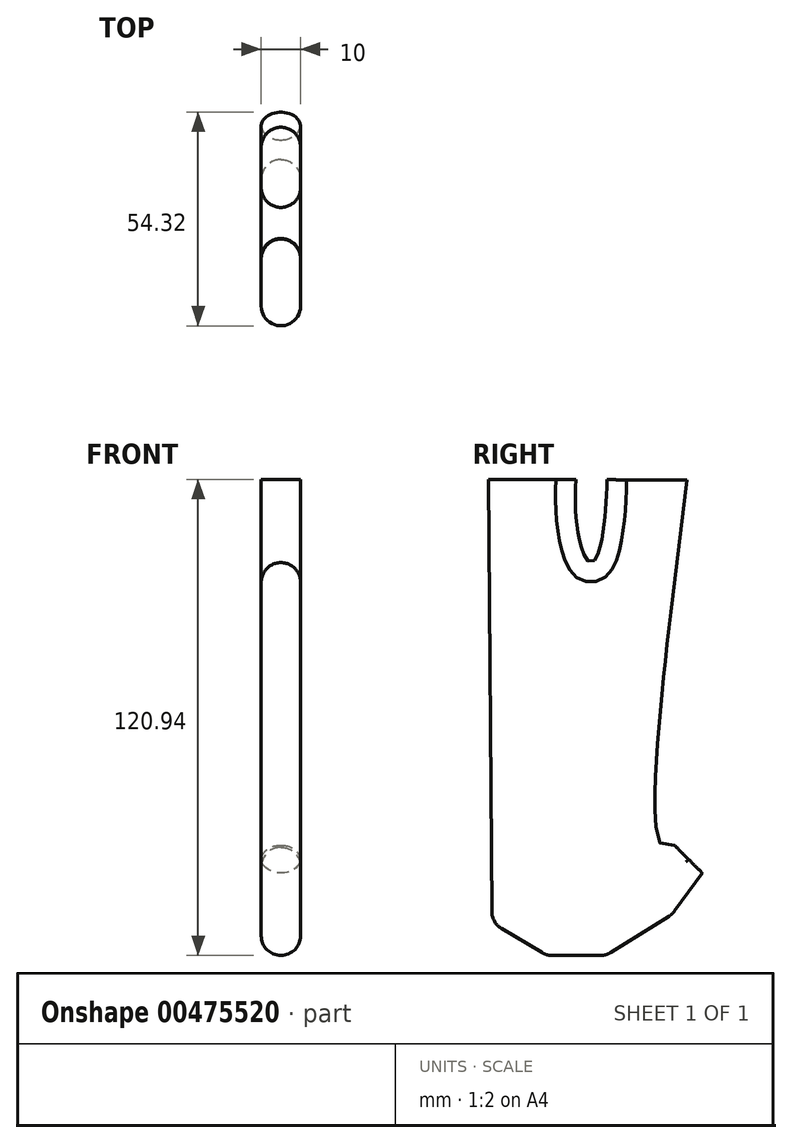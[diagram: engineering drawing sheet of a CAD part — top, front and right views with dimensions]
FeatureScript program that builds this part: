
annotation { "Feature Type Name" : "Feature", "Feature Type Description" : "" }
export const myFeature = defineFeature(function(context is Context, id is Id, definition is map)
    precondition{}
    {
        {
            var Q0;
            Q0=qCreatedBy(makeId("Top.planeOp"),FACE);
            var sketch = newSketch(context, id + "F0", { "sketchPlane" : qUnion([Q0])});
            skLineSegment(sketch, "E0.bottom", {"start": v(50, 50) * mm, "end": v(-50, 50) * mm});
            skLineSegment(sketch, "E0.top", {"start": v(50, -50) * mm, "end": v(-50, -50) * mm});
            skLineSegment(sketch, "E0.left", {"start": v(50, 50) * mm, "end": v(50, -50) * mm});
            skLineSegment(sketch, "E0.right", {"start": v(-50, 50) * mm, "end": v(-50, -50) * mm});
            skPoint(sketch, "E0.middle", {"position": v(0, 0) * mm});
            skSolve(sketch);
        }
        {
            var Q0;
            Q0=qCreatedBy(makeId("Right.planeOp"),FACE);
            var sketch = newSketch(context, id + "F1", { "sketchPlane" : qUnion([Q0])});
            skLineSegment(sketch, "E1", {"start": v(32.93, -92.93) * mm, "end": v(40, -100) * mm});
            skLineSegment(sketch, "E2", {"start": v(40, -100) * mm, "end": v(50, -100) * mm});
            skLineSegment(sketch, "E3", {"start": v(50, -100) * mm, "end": v(50, 0) * mm});
            skLineSegment(sketch, "E4", {"start": v(40, -100) * mm, "end": v(32.42, -110.44) * mm});
            skLineSegment(sketch, "E5", {"start": v(32.42, -110.44) * mm, "end": v(15.56, -120.94) * mm});
            skLineSegment(sketch, "E6", {"start": v(15.56, -120.94) * mm, "end": v(0.42, -120.94) * mm});
            skLineSegment(sketch, "E7", {"start": v(0.42, -120.94) * mm, "end": v(-13.45, -112.58) * mm});
            skLineSegment(sketch, "E8", {"start": v(-13.45, -112.58) * mm, "end": v(-14.32, 0) * mm});
            skLineSegment(sketch, "E9", {"start": v(7.9, -0.07) * mm, "end": v(-14.32, 0) * mm});
            skLineSegment(sketch, "E10", {"start": v(15.79, -0.07) * mm, "end": v(36.15, -0.14) * mm});
            skFitSpline(sketch, "E11", {"points": [v(32.93, -92.93) * mm, v(29.65, -92.93) * mm, v(36.15, -0.14) * mm], "startDerivative": vector(-23, -8.71) * mm, "endDerivative": vector(19.71, 156.62) * mm});
            skFitSpline(sketch, "E12", {"points": [v(15.79, -0.07) * mm, v(11.46, -21.08) * mm, v(7.9, -0.07) * mm], "startDerivative": vector(-1.65, -83.3) * mm, "endDerivative": vector(4.4, 67.18) * mm});
            skSolve(sketch);
        }
        {
            var Q0;
            Q0=makeQuery(id+"F1.imprint","IMPRINT",FACE,{"disambiguationData":[TD([[makeQuery(id+"F1.imprint","IMPRINT",EDGE,{"derivedFrom":sQuery(id+"F1.wireOp",EDGE,"E1")}),-1.0]])]});
            extrude(context, id + "F2", {"entities" : qUnion([Q0]), "endBound" : BoundingType.SYMMETRIC, "depth" : 10 * mm});
        }
        {
            var Q0;
            Q0=makeQuery(id+"F2.opExtrude","CAP_EDGE",EDGE,{"disambiguationData":[OSD([sQuery(id+"F1.wireOp",EDGE,"E7")])],"isStart":false});
            var Q1;
            Q1=makeQuery(id+"F2.opExtrude","CAP_EDGE",EDGE,{"disambiguationData":[OSD([sQuery(id+"F1.wireOp",EDGE,"E6")])],"isStart":false});
            var Q2;
            Q2=makeQuery(id+"F2.opExtrude","CAP_EDGE",EDGE,{"disambiguationData":[OSD([sQuery(id+"F1.wireOp",EDGE,"E5")])],"isStart":false});
            var Q3;
            Q3=makeQuery(id+"F2.opExtrude","CAP_EDGE",EDGE,{"disambiguationData":[OSD([sQuery(id+"F1.wireOp",EDGE,"E4")])],"isStart":false});
            var Q4;
            Q4=makeQuery(id+"F2.opExtrude","CAP_EDGE",EDGE,{"disambiguationData":[OSD([sQuery(id+"F1.wireOp",EDGE,"49eb233f-eca1-4608-b86e-9a41fd80e5eb")])],"isStart":false});
            var Q5;
            Q5=makeQuery(id+"F2.opExtrude","CAP_EDGE",EDGE,{"disambiguationData":[OSD([sQuery(id+"F1.wireOp",EDGE,"zjXfg7Vx-LYZx-WJwB-u50H-vYy3XpUTTi9i")])],"isStart":false});
            var Q6;
            Q6=makeQuery(id+"F2.opExtrude","CAP_EDGE",EDGE,{"disambiguationData":[OSD([sQuery(id+"F1.wireOp",EDGE,"E5")])],"isStart":true});
            var Q7;
            Q7=makeQuery(id+"F2.opExtrude","CAP_EDGE",EDGE,{"disambiguationData":[OSD([sQuery(id+"F1.wireOp",EDGE,"E6")])],"isStart":true});
            var Q8;
            Q8=makeQuery(id+"F2.opExtrude","CAP_EDGE",EDGE,{"disambiguationData":[OSD([sQuery(id+"F1.wireOp",EDGE,"E7")])],"isStart":true});
            var Q9;
            Q9=makeQuery(id+"F2.opExtrude","CAP_EDGE",EDGE,{"disambiguationData":[OSD([sQuery(id+"F1.wireOp",EDGE,"E4")])],"isStart":true});
            var Q10;
            Q10=makeQuery(id+"F2.opExtrude","CAP_EDGE",EDGE,{"disambiguationData":[OSD([sQuery(id+"F1.wireOp",EDGE,"49eb233f-eca1-4608-b86e-9a41fd80e5eb")])],"isStart":true});
            var Q11;
            Q11=makeQuery(id+"F2.opExtrude","CAP_EDGE",EDGE,{"disambiguationData":[OSD([sQuery(id+"F1.wireOp",EDGE,"E8")])],"isStart":true});
            var Q12;
            Q12=makeQuery(id+"F2.opExtrude","CAP_EDGE",EDGE,{"disambiguationData":[OSD([sQuery(id+"F1.wireOp",EDGE,"zjXfg7Vx-LYZx-WJwB-u50H-vYy3XpUTTi9i")])],"isStart":true});
            var Q13;
            Q13=makeQuery(id+"F2.opExtrude","SWEPT_FACE",FACE,{"disambiguationData":[OSD([sQuery(id+"F1.wireOp",EDGE,"E5")])]});
            var Q14;
            Q14=makeQuery(id+"F2.opExtrude","SWEPT_EDGE",EDGE,{"disambiguationData":[OSD([sQuery(id+"F1.wireOp",EDGE,"E6"),sQuery(id+"F1.wireOp",EDGE,"E7")])]});
            var Q15;
            Q15=makeQuery(id+"F2.opExtrude","SWEPT_EDGE",EDGE,{"disambiguationData":[OSD([sQuery(id+"F1.wireOp",EDGE,"E7"),sQuery(id+"F1.wireOp",EDGE,"E8")])]});
            var Q16;
            Q16=makeQuery(id+"F2.opExtrude","CAP_EDGE",EDGE,{"disambiguationData":[OSD([sQuery(id+"F1.wireOp",EDGE,"44457354-6a0a-461b-9640-03c7e871ec64")])],"isStart":false});
            var Q17;
            Q17=makeQuery(id+"F2.opExtrude","CAP_EDGE",EDGE,{"disambiguationData":[OSD([sQuery(id+"F1.wireOp",EDGE,"IOLs24wW-nGt2-bCdK-CUzV-omeq2doUS0Fj")])],"isStart":false});
            var Q18;
            Q18=makeQuery(id+"F2.opExtrude","CAP_EDGE",EDGE,{"disambiguationData":[OSD([sQuery(id+"F1.wireOp",EDGE,"ep5JJxwo-5Ehf-mu99-rTiO-K8ae0PhvzPRr")])],"isStart":false});
            var Q19;
            Q19=makeQuery(id+"F2.opExtrude","CAP_EDGE",EDGE,{"disambiguationData":[OSD([sQuery(id+"F1.wireOp",EDGE,"nmbZKGiq-SK3K-He9k-tR5C-gfZI34xlJpe3")])],"isStart":false});
            var Q20;
            Q20=makeQuery(id+"F2.opExtrude","CAP_EDGE",EDGE,{"disambiguationData":[OSD([sQuery(id+"F1.wireOp",EDGE,"44457354-6a0a-461b-9640-03c7e871ec64")])],"isStart":true});
            var Q21;
            Q21=makeQuery(id+"F2.opExtrude","CAP_EDGE",EDGE,{"disambiguationData":[OSD([sQuery(id+"F1.wireOp",EDGE,"ep5JJxwo-5Ehf-mu99-rTiO-K8ae0PhvzPRr")])],"isStart":true});
            var Q22;
            Q22=makeQuery(id+"F2.opExtrude","CAP_EDGE",EDGE,{"disambiguationData":[OSD([sQuery(id+"F1.wireOp",EDGE,"nmbZKGiq-SK3K-He9k-tR5C-gfZI34xlJpe3")])],"isStart":true});
            var Q23;
            Q23=makeQuery(id+"F2.opExtrude","CAP_EDGE",EDGE,{"disambiguationData":[OSD([sQuery(id+"F1.wireOp",EDGE,"IOLs24wW-nGt2-bCdK-CUzV-omeq2doUS0Fj")])],"isStart":true});
            var Q24;
            Q24=makeQuery(id+"F2.opExtrude","CAP_EDGE",EDGE,{"disambiguationData":[OSD([sQuery(id+"F1.wireOp",EDGE,"1a2d0c1b-d173-4b5c-91dd-a013b25bc349")])],"isStart":true});
            var Q25;
            Q25=makeQuery(id+"F2.opExtrude","SWEPT_EDGE",EDGE,{"disambiguationData":[OSD([sQuery(id+"F1.wireOp",EDGE,"ctv6Uj9i-5GiC-c2g8-MQwH-dTNLdzQty9C9"),sQuery(id+"F1.wireOp",EDGE,"01453e82-e355-43f1-b94c-4e8e36261eb0")])]});
            var Q26;
            Q26=makeQuery(id+"F2.opExtrude","CAP_EDGE",EDGE,{"disambiguationData":[OSD([sQuery(id+"F1.wireOp",EDGE,"E11")])],"isStart":false});
            var Q27;
            Q27=makeQuery(id+"F2.opExtrude","CAP_EDGE",EDGE,{"disambiguationData":[OSD([sQuery(id+"F1.wireOp",EDGE,"E11")])],"isStart":true});
            var Q28;
            Q28=makeQuery(id+"F2.opExtrude","CAP_EDGE",EDGE,{"disambiguationData":[OSD([sQuery(id+"F1.wireOp",EDGE,"E12")])],"isStart":true});
            var Q29;
            Q29=makeQuery(id+"F2.opExtrude","CAP_EDGE",EDGE,{"disambiguationData":[OSD([sQuery(id+"F1.wireOp",EDGE,"E12")])],"isStart":false});
            var Q30;
            Q30=makeQuery(id+"F2.opExtrude","CAP_EDGE",EDGE,{"disambiguationData":[OSD([sQuery(id+"F1.wireOp",EDGE,"E8")])],"isStart":false});
            fillet(context, id + "F3", {"entities" : qUnion([Q0, Q1, Q2, Q3, Q4, Q5, Q6, Q7, Q8, Q9, Q10, Q11, Q12, Q13, Q14, Q15, Q16, Q17, Q18, Q19, Q20, Q21, Q22, Q23, Q24, Q25, Q26, Q27, Q28, Q29, Q30]), "radius" : 5 * mm, "tangentPropagation" : true, "allowEdgeOverflow" : false});
        }
    });
